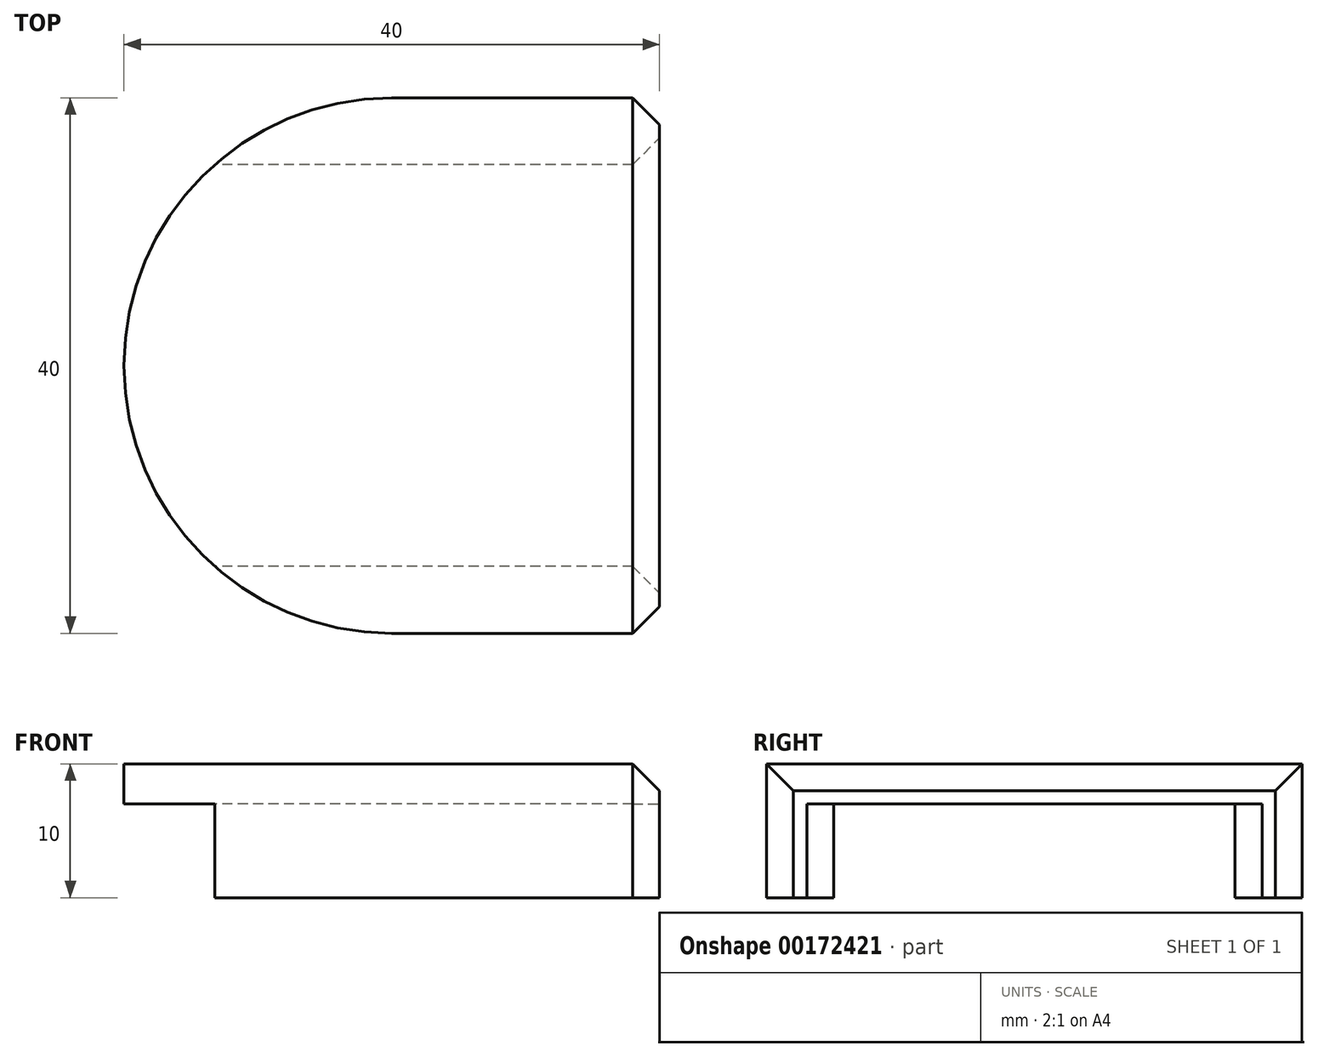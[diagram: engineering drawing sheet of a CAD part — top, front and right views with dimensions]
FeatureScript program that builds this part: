
annotation { "Feature Type Name" : "Feature", "Feature Type Description" : "" }
export const myFeature = defineFeature(function(context is Context, id is Id, definition is map)
    precondition{}
    {
        {
            var Q0;
            Q0=qCreatedBy(makeId("Top.planeOp"),FACE);
            var sketch = newSketch(context, id + "F0", { "sketchPlane" : qUnion([Q0])});
            skLineSegment(sketch, "E0.bottom", {"start": v(-20, 20) * mm, "end": v(20, 20) * mm});
            skLineSegment(sketch, "E0.top", {"start": v(-20, -20) * mm, "end": v(20, -20) * mm});
            skLineSegment(sketch, "E0.left", {"start": v(-20, 20) * mm, "end": v(-20, -20) * mm});
            skLineSegment(sketch, "E0.right", {"start": v(20, 20) * mm, "end": v(20, -20) * mm});
            skPoint(sketch, "E0.middle", {"position": v(0, 0) * mm});
            skSolve(sketch);
        }
        {
            var Q0;
            Q0 = qSketchRegion(id + "F0", true);
            extrude(context, id + "F1", {"entities" : qUnion([Q0]), "depth" : 3 * mm});
        }
        {
            var Q0;
            Q0=makeQuery(id+"F1.opExtrude","CAP_FACE",FACE,{"disambiguationData":[OSD([sQuery(id+"F0.wireOp",EDGE,"E0.bottom"),sQuery(id+"F0.wireOp",EDGE,"E0.top"),sQuery(id+"F0.wireOp",EDGE,"E0.left"),sQuery(id+"F0.wireOp",EDGE,"E0.right")])],"isStart":true});
            var sketch = newSketch(context, id + "F2", { "sketchPlane" : qUnion([Q0])});
            skLineSegment(sketch, "E1.bottom", {"start": v(20, 20) * mm, "end": v(-20, 20) * mm});
            skLineSegment(sketch, "E1.top", {"start": v(20, 15) * mm, "end": v(-20, 15) * mm});
            skLineSegment(sketch, "E1.left", {"start": v(20, 20) * mm, "end": v(20, 15) * mm});
            skLineSegment(sketch, "E1.right", {"start": v(-20, 20) * mm, "end": v(-20, 15) * mm});
            skPoint(sketch, "E1.middle", {"position": v(0, 17.5) * mm});
            skPoint(sketch, "E1.middle.positionSnap0", {"position": v(0, 20) * mm});
            skPoint(sketch, "E1.centerSnap0", {"position": v(0, 20) * mm});
            skLineSegment(sketch, "E2.bottom", {"start": v(20, -20) * mm, "end": v(-20, -20) * mm});
            skLineSegment(sketch, "E2.top", {"start": v(20, -15) * mm, "end": v(-20, -15) * mm});
            skLineSegment(sketch, "E2.left", {"start": v(20, -20) * mm, "end": v(20, -15) * mm});
            skLineSegment(sketch, "E2.right", {"start": v(-20, -20) * mm, "end": v(-20, -15) * mm});
            skPoint(sketch, "E2.middle", {"position": v(0, -17.5) * mm});
            skSolve(sketch);
        }
        {
            var Q0;
            Q0 = qSketchRegion(id + "F2", true);
            extrude(context, id + "F3", {"entities" : qUnion([Q0]), "operationType" : NewBodyOperationType.ADD, "depth" : 7 * mm});
        }
        {
            var Q0;
            Q0=makeQuery(id+"F3.boolean.opBoolean","MERGE",EDGE,{"derivedFrom":[makeQuery(id+"F1.opExtrude","SWEPT_EDGE",EDGE,{"disambiguationData":[OSD([sQuery(id+"F0.wireOp",EDGE,"E0.bottom"),sQuery(id+"F0.wireOp",EDGE,"E0.left")])]}),makeQuery(id+"F3.opExtrude","SWEPT_EDGE",EDGE,{"disambiguationData":[OSD([sQuery(id+"F2.wireOp",EDGE,"E2.bottom"),sQuery(id+"F2.wireOp",EDGE,"E2.right")])]})]});
            var Q1;
            Q1=makeQuery(id+"F3.boolean.opBoolean","MERGE",EDGE,{"derivedFrom":[makeQuery(id+"F1.opExtrude","SWEPT_EDGE",EDGE,{"disambiguationData":[OSD([sQuery(id+"F0.wireOp",EDGE,"E0.top"),sQuery(id+"F0.wireOp",EDGE,"E0.left")])]}),makeQuery(id+"F3.opExtrude","SWEPT_EDGE",EDGE,{"disambiguationData":[OSD([sQuery(id+"F2.wireOp",EDGE,"E1.bottom"),sQuery(id+"F2.wireOp",EDGE,"E1.right")])]})]});
            fillet(context, id + "F4", {"entities" : qUnion([Q0, Q1]), "radius" : 20 * mm, "tangentPropagation" : true, "allowEdgeOverflow" : false});
        }
        {
            var Q0;
            {var subQ0=sQuery(id+"F0.wireOp",EDGE,"E0.left");var subQ1=sQuery(id+"F0.wireOp",EDGE,"E0.top");Q0=makeQuery(id+"F4.opFillet","BLEND_EDGE",EDGE,{"blendedFrom":[makeQuery(id+"F3.boolean.opBoolean","MERGE",EDGE,{"derivedFrom":[makeQuery(id+"F1.opExtrude","SWEPT_EDGE",EDGE,{"disambiguationData":[OSD([subQ1,subQ0])]}),makeQuery(id+"F3.opExtrude","SWEPT_EDGE",EDGE,{"disambiguationData":[OSD([sQuery(id+"F2.wireOp",EDGE,"E1.bottom"),sQuery(id+"F2.wireOp",EDGE,"E1.right")])]})]}),makeQuery(id+"F1.opExtrude","CAP_FACE",FACE,{"disambiguationData":[OSD([sQuery(id+"F0.wireOp",EDGE,"E0.bottom"),subQ1,subQ0,sQuery(id+"F0.wireOp",EDGE,"E0.right")])],"isStart":false})],"blendedInto":[makeQuery(id+"F1.opExtrude","CAP_FACE",FACE,{"disambiguationData":[OSD([sQuery(id+"F0.wireOp",EDGE,"E0.bottom"),subQ1,subQ0,sQuery(id+"F0.wireOp",EDGE,"E0.right")])],"isStart":false})]});}
            var Q1;
            Q1=makeQuery(id+"F3.boolean.opBoolean","MERGE",EDGE,{"derivedFrom":[makeQuery(id+"F1.opExtrude","SWEPT_EDGE",EDGE,{"disambiguationData":[OSD([sQuery(id+"F0.wireOp",EDGE,"E0.top"),sQuery(id+"F0.wireOp",EDGE,"E0.right")])]}),makeQuery(id+"F3.opExtrude","SWEPT_EDGE",EDGE,{"disambiguationData":[OSD([sQuery(id+"F2.wireOp",EDGE,"E1.bottom"),sQuery(id+"F2.wireOp",EDGE,"E1.left")])]})]});
            var Q2;
            Q2=makeQuery(id+"F1.opExtrude","CAP_EDGE",EDGE,{"disambiguationData":[OSD([sQuery(id+"F0.wireOp",EDGE,"E0.right")])],"isStart":false});
            var Q3;
            Q3=makeQuery(id+"F3.boolean.opBoolean","MERGE",EDGE,{"derivedFrom":[makeQuery(id+"F1.opExtrude","SWEPT_EDGE",EDGE,{"disambiguationData":[OSD([sQuery(id+"F0.wireOp",EDGE,"E0.bottom"),sQuery(id+"F0.wireOp",EDGE,"E0.right")])]}),makeQuery(id+"F3.opExtrude","SWEPT_EDGE",EDGE,{"disambiguationData":[OSD([sQuery(id+"F2.wireOp",EDGE,"E2.bottom"),sQuery(id+"F2.wireOp",EDGE,"E2.left")])]})]});
            var Q4;
            Q4=makeQuery(id+"F3.opExtrude","SWEPT_EDGE",EDGE,{"disambiguationData":[OSD([sQuery(id+"F0.wireOp",EDGE,"E0.right"),sQuery(id+"F2.wireOp",EDGE,"E2.top"),sQuery(id+"F2.wireOp",EDGE,"E2.left")])]});
            var Q5;
            Q5=makeQuery(id+"F3.opExtrude","SWEPT_EDGE",EDGE,{"disambiguationData":[OSD([sQuery(id+"F0.wireOp",EDGE,"E0.right"),sQuery(id+"F2.wireOp",EDGE,"E1.top"),sQuery(id+"F2.wireOp",EDGE,"E1.left")])]});
            chamfer(context, id + "F5", {"entities" : qUnion([Q0, Q1, Q2, Q3, Q4, Q5]), "width" : 2 * mm, "tangentPropagation" : true});
        }
    });
